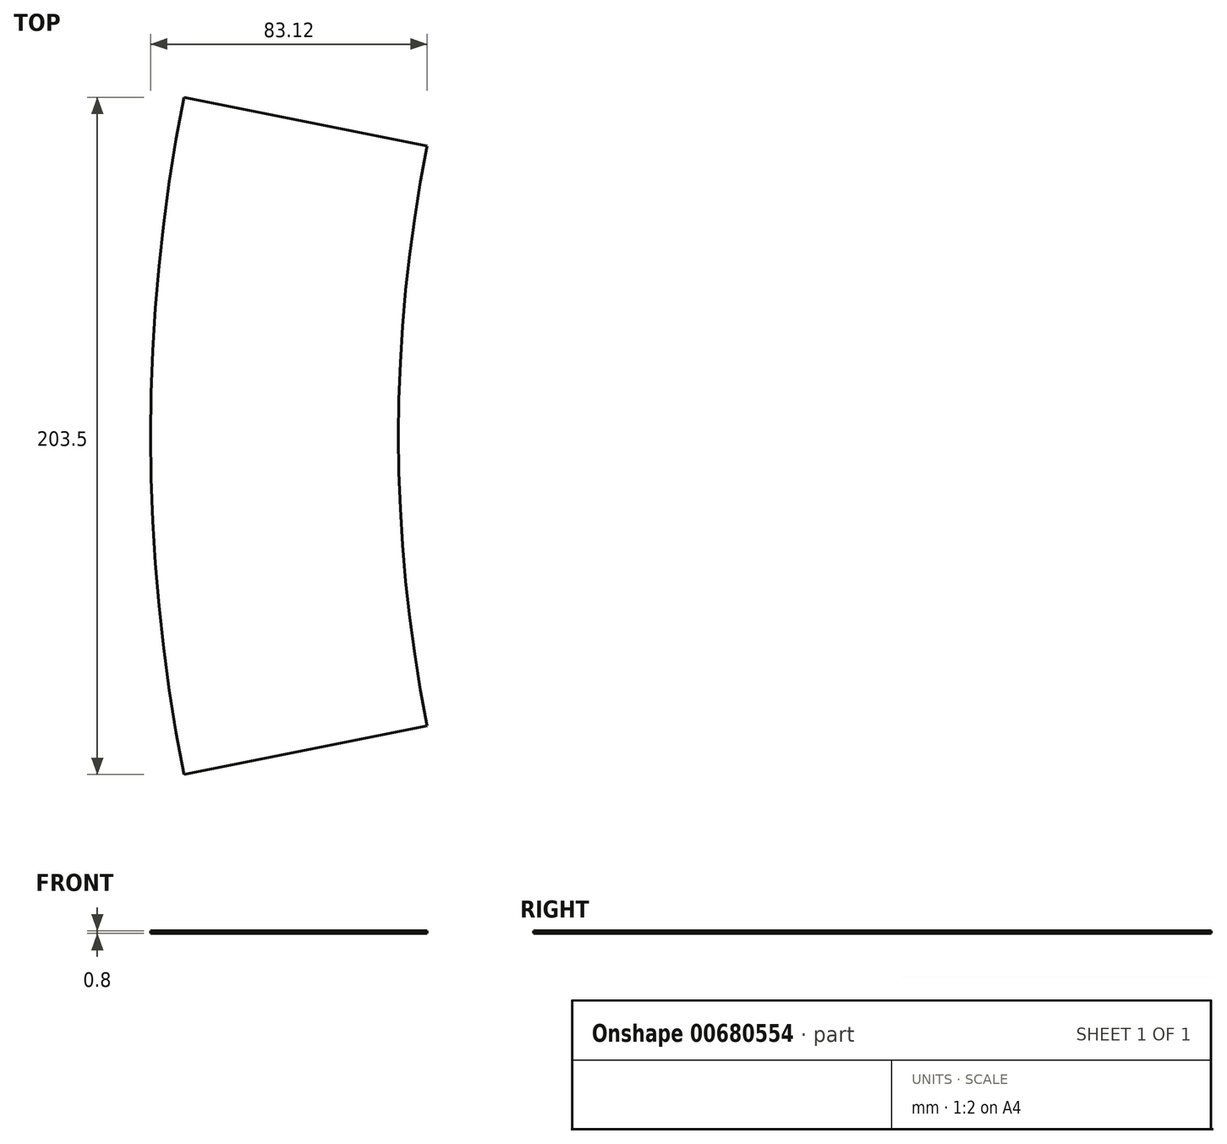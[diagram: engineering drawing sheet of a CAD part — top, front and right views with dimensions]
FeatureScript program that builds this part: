
annotation { "Feature Type Name" : "Feature", "Feature Type Description" : "" }
export const myFeature = defineFeature(function(context is Context, id is Id, definition is map)
    precondition{}
    {
        {
            var Q0;
            Q0=qCreatedBy(makeId("Front.planeOp"),FACE);
            var sketch = newSketch(context, id + "F0", { "sketchPlane" : qUnion([Q0])});
            skLineSegment(sketch, "E0.bottom", {"start": v(40.75, 0) * mm, "end": v(115.25, 0) * mm});
            skLineSegment(sketch, "E0.top", {"start": v(40.75, 0.8) * mm, "end": v(115.25, 0.8) * mm});
            skLineSegment(sketch, "E0.left", {"start": v(40.75, 0) * mm, "end": v(40.75, 0.8) * mm});
            skLineSegment(sketch, "E0.right", {"start": v(115.25, 0) * mm, "end": v(115.25, 0.8) * mm});
            skLineSegment(sketch, "E1", {"start": v(560, 40.53) * mm, "end": v(560, -28.06) * mm});
            skSolve(sketch);
        }
        {
            var Q0;
            Q0=makeQuery(id+"F0.imprint","IMPRINT",FACE,{"disambiguationData":[TD([[makeQuery(id+"F0.imprint","IMPRINT",EDGE,{"derivedFrom":sQuery(id+"F0.wireOp",EDGE,"E0.bottom")}),1.0]])]});
            var Q1;
            Q1=sQuery(id+"F0.wireOp",EDGE,"E1");
            revolve(context, id + "F1", {"entities" : qUnion([Q0]), "axis" : qUnion([Q1]), "revolveType" : RevolveType.SYMMETRIC, "angle" : 22.6 * degree});
        }
    });
